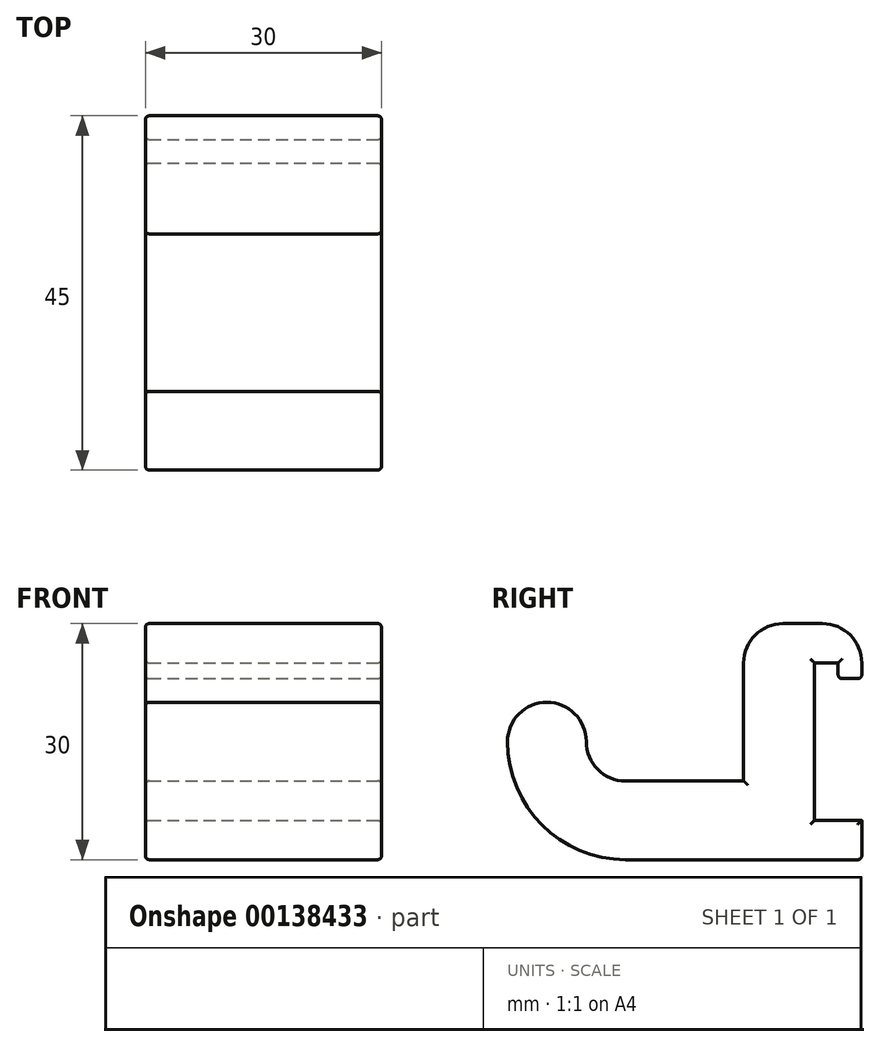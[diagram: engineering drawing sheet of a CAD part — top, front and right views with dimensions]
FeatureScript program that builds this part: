
annotation { "Feature Type Name" : "Feature", "Feature Type Description" : "" }
export const myFeature = defineFeature(function(context is Context, id is Id, definition is map)
    precondition{}
    {
        {
            var Q0;
            Q0=qCreatedBy(makeId("Front.planeOp"),FACE);
            var sketch = newSketch(context, id + "F0", { "sketchPlane" : qUnion([Q0])});
            skLineSegment(sketch, "E0.bottom", {"start": v(0, 0) * mm, "end": v(30, 0) * mm});
            skLineSegment(sketch, "E0.top", {"start": v(0, 30) * mm, "end": v(30, 30) * mm});
            skLineSegment(sketch, "E0.left", {"start": v(0, 0) * mm, "end": v(0, 30) * mm});
            skLineSegment(sketch, "E0.right", {"start": v(30, 0) * mm, "end": v(30, 30) * mm});
            skSolve(sketch);
        }
        {
            var Q0;
            Q0=qSketchRegion(id+"F0",true);
            extrude(context, id + "F1", {"entities" : qUnion([Q0]), "depth" : 15 * mm});
        }
        {
            var Q0;
            Q0=makeQuery(id+"F1.opExtrude","SWEPT_FACE",FACE,{"disambiguationData":[OSD([sQuery(id+"F0.wireOp",EDGE,"E0.right")])]});
            var sketch = newSketch(context, id + "F2", { "sketchPlane" : qUnion([Q0])});
            skLineSegment(sketch, "E1", {"start": v(0, 5) * mm, "end": v(-6, 5) * mm});
            skLineSegment(sketch, "E2", {"start": v(-6, 5) * mm, "end": v(-6, 25) * mm});
            skLineSegment(sketch, "E3", {"start": v(-6, 25) * mm, "end": v(-3, 25) * mm});
            skLineSegment(sketch, "E4", {"start": v(-3, 25) * mm, "end": v(-3, 23) * mm});
            skLineSegment(sketch, "E5", {"start": v(-3, 23) * mm, "end": v(0, 23) * mm});
            skLineSegment(sketch, "E6", {"start": v(0, 23) * mm, "end": v(0, 5) * mm});
            skSolve(sketch);
        }
        {
            var Q0;
            Q0=qSketchRegion(id+"F2",true);
            extrude(context, id + "F3", {"entities" : qUnion([Q0]), "operationType" : NewBodyOperationType.REMOVE, "endBound" : BoundingType.THROUGH_ALL, "oppositeDirection" : true, "depth" : 25 * mm});
        }
        {
            var Q0;
            Q0=makeQuery(id+"F1.opExtrude","SWEPT_FACE",FACE,{"disambiguationData":[OSD([sQuery(id+"F0.wireOp",EDGE,"E0.right")])]});
            var sketch = newSketch(context, id + "F4", { "sketchPlane" : qUnion([Q0])});
            skLineSegment(sketch, "E7", {"start": v(-15, 0) * mm, "end": v(-30, 0) * mm});
            skArc(sketch, "E8", {"start": v(-30, 0) * mm, "mid": v(-40.6, 4.4) * mm, "end": v(-45, 15) * mm});
            skLineSegment(sketch, "E9", {"start": v(-15, 10) * mm, "end": v(-30, 10) * mm});
            skArc(sketch, "E10", {"start": v(-30, 10) * mm, "mid": v(-33.54, 11.46) * mm, "end": v(-35, 15) * mm});
            skArc(sketch, "E11", {"start": v(-45, 15) * mm, "mid": v(-40, 20) * mm, "end": v(-35, 15) * mm});
            skLineSegment(sketch, "E12", {"start": v(-17.67, 15) * mm, "end": v(-47.33, 15) * mm, "construction": true});
            skSolve(sketch);
        }
        {
            var Q0;
            Q0 = qSketchRegion(id + "F4", true);
            var Q1;
            {var subQ1=sQuery(id+"F4.wireOp",EDGE,"E7");Q1=makeQuery(id+"F4.imprint","IMPRINT",FACE,{"disambiguationData":[TD([[makeQuery(id+"F4.imprint","IMPRINT",EDGE,{"derivedFrom":subQ1}),-1.0]])]});}
            var Q2;
            Q2=makeQuery(id+"F1.opExtrude","SWEPT_FACE",FACE,{"disambiguationData":[OSD([sQuery(id+"F0.wireOp",EDGE,"E0.left")])]});
            extrude(context, id + "F5", {"entities" : qUnion([Q0, Q1]), "operationType" : NewBodyOperationType.ADD, "endBound" : BoundingType.UP_TO_SURFACE, "oppositeDirection" : true, "endBoundEntityFace" : qUnion([Q2]), "depth" : 25 * mm});
        }
        {
            var Q0;
            Q0=makeQuery(id+"F5.opExtrude","SWEPT_EDGE",EDGE,{"disambiguationData":[OSD([sQuery(id+"F0.wireOp",EDGE,"E0.right"),sQuery(id+"F4.wireOp",EDGE,"E9")])]});
            var Q1;
            Q1=makeQuery(id+"F1.opExtrude","CAP_EDGE",EDGE,{"disambiguationData":[OSD([sQuery(id+"F0.wireOp",EDGE,"E0.top")])],"isStart":false});
            var Q2;
            Q2=makeQuery(id+"F1.opExtrude","CAP_EDGE",EDGE,{"disambiguationData":[OSD([sQuery(id+"F0.wireOp",EDGE,"E0.top")])],"isStart":true});
            fillet(context, id + "F6", {"entities" : qUnion([Q0, Q1, Q2]), "radius" : 5 * mm, "tangentPropagation" : true, "allowEdgeOverflow" : false});
        }
        {
            var Q0;
            {var subQ0=sQuery(id+"F0.wireOp",EDGE,"E0.right");Q0=makeQuery(id+"F5.boolean.opBoolean","MERGE",FACE,{"derivedFrom":[makeQuery(id+"F1.opExtrude","SWEPT_FACE",FACE,{"disambiguationData":[OSD([subQ0])]}),makeQuery(id+"F5.opExtrude","CAP_FACE",FACE,{"disambiguationData":[OSD([subQ0,sQuery(id+"F4.wireOp",EDGE,"E7"),sQuery(id+"F4.wireOp",EDGE,"E8"),sQuery(id+"F4.wireOp",EDGE,"E9"),sQuery(id+"F4.wireOp",EDGE,"E10"),sQuery(id+"F4.wireOp",EDGE,"E11")])],"isStart":true})]});}
            var Q1;
            {var subQ0=sQuery(id+"F0.wireOp",EDGE,"E0.left");Q1=makeQuery(id+"F5.boolean.opBoolean","MERGE",FACE,{"derivedFrom":[makeQuery(id+"F1.opExtrude","SWEPT_FACE",FACE,{"disambiguationData":[OSD([subQ0])]}),makeQuery(id+"F5.opExtrude","CAP_FACE",FACE,{"disambiguationData":[OSD([subQ0])],"isStart":false})]});}
            fillet(context, id + "F7", {"entities" : qUnion([Q0, Q1]), "radius" : 0.5 * mm, "tangentPropagation" : true, "allowEdgeOverflow" : false});
        }
        {
            var Q0;
            Q0=makeQuery(id+"F3.boolean.opBoolean","COPY",EDGE,{"derivedFrom":makeQuery(id+"F3.opExtrude","SWEPT_EDGE",EDGE,{"disambiguationData":[OSD([sQuery(id+"F0.wireOp",EDGE,"E0.right"),sQuery(id+"F2.wireOp",EDGE,"E1"),sQuery(id+"F2.wireOp",EDGE,"E6")])]})});
            var Q1;
            Q1=makeQuery(id+"F1.opExtrude","CAP_EDGE",EDGE,{"disambiguationData":[OSD([sQuery(id+"F0.wireOp",EDGE,"E0.bottom")])],"isStart":true});
            var Q2;
            Q2=makeQuery(id+"F3.boolean.opBoolean","COPY",EDGE,{"derivedFrom":makeQuery(id+"F3.opExtrude","SWEPT_EDGE",EDGE,{"disambiguationData":[OSD([sQuery(id+"F0.wireOp",EDGE,"E0.right"),sQuery(id+"F2.wireOp",EDGE,"E5"),sQuery(id+"F2.wireOp",EDGE,"E6")])]})});
            var Q3;
            Q3=makeQuery(id+"F3.boolean.opBoolean","COPY",EDGE,{"derivedFrom":makeQuery(id+"F3.opExtrude","SWEPT_EDGE",EDGE,{"disambiguationData":[OSD([sQuery(id+"F2.wireOp",EDGE,"E4"),sQuery(id+"F2.wireOp",EDGE,"E5")])]})});
            fillet(context, id + "F8", {"entities" : qUnion([Q0, Q1, Q2, Q3]), "radius" : 0.5 * mm, "tangentPropagation" : true, "allowEdgeOverflow" : false});
        }
    });
